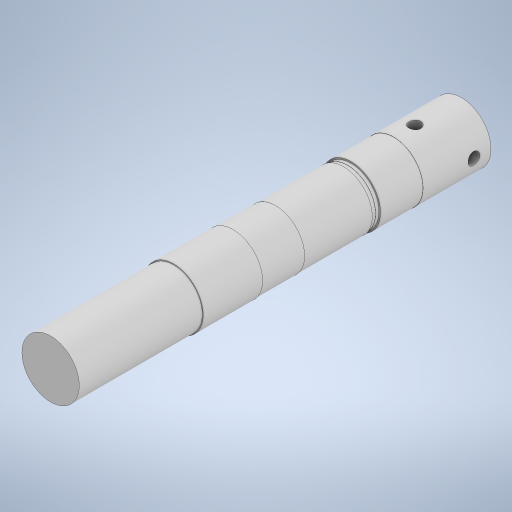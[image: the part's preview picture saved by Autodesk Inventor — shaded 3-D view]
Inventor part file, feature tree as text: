
AUTODESK INVENTOR PART (.ipt)
format: ipt  version: 2024 (Build 280153000, 153)  size: 329,728 bytes
history: native  units: mm
features: sketch x6, extrude x3, plane x1, revolve x1
ambient origin geometry x8: Origin, YZ Plane, XZ Plane, XY Plane, X Axis, Y Axis, Z Axis, Center Point
bodies: Body1 (feature_tree)
feature tree (11):
  sketch  "Sketch1"  dims[d0=105.0mm d3=70.0mm]
  plane  "Work Plane1"
  sketch  "Sketch2"  dims[d2=80.0mm d4=5.0mm]
  sketch  "Sketch3"  dims[d5=4.0mm d6=50.0mm]
  sketch  "Sketch4"  dims[d15=40.0mm d16=50.0mm]
  revolve  "Revolution1"  [1 undecoded]
  extrude  "Extrusion4"  Depth=5.0mm
  extrude  "Extrusion5"  Depth=50.0mm
  extrude  "Extrusion6"  Depth=50.0mm
  sketch  "Sketch5"  dims[d17=15.0mm]
  sketch  "Sketch6"  dims[d18=10.0mm d19=10.0mm d22=14.0mm d28=14.0mm d31=90.0deg d32=10.0mm d33=0.0mm d34=20.0mm d35=45.0mm d36=0.0mm d37=0.0mm d38=35.0mm d39=30.0mm d40=0.0mm d41=0.0mm d65=259.0mm d66=79.0mm d67=114.0mm d68=75.0mm d69=33.75mm d70=34.75mm d71=33.95mm d78=32.75mm d82=4.0mm d83=50.0mm d84=32.95mm d85=34.85mm d86=80.0mm d87=33.75mm d88=34.25mm d89=34.65mm d20=0.5mm d21=0.872665mm d23=0.872665mm]
note: 1 required parameter value undecoded (feature->parameter linkage not recoverable at this tier; creation-order binding heuristic only, values carry confidence <= 0.55)
